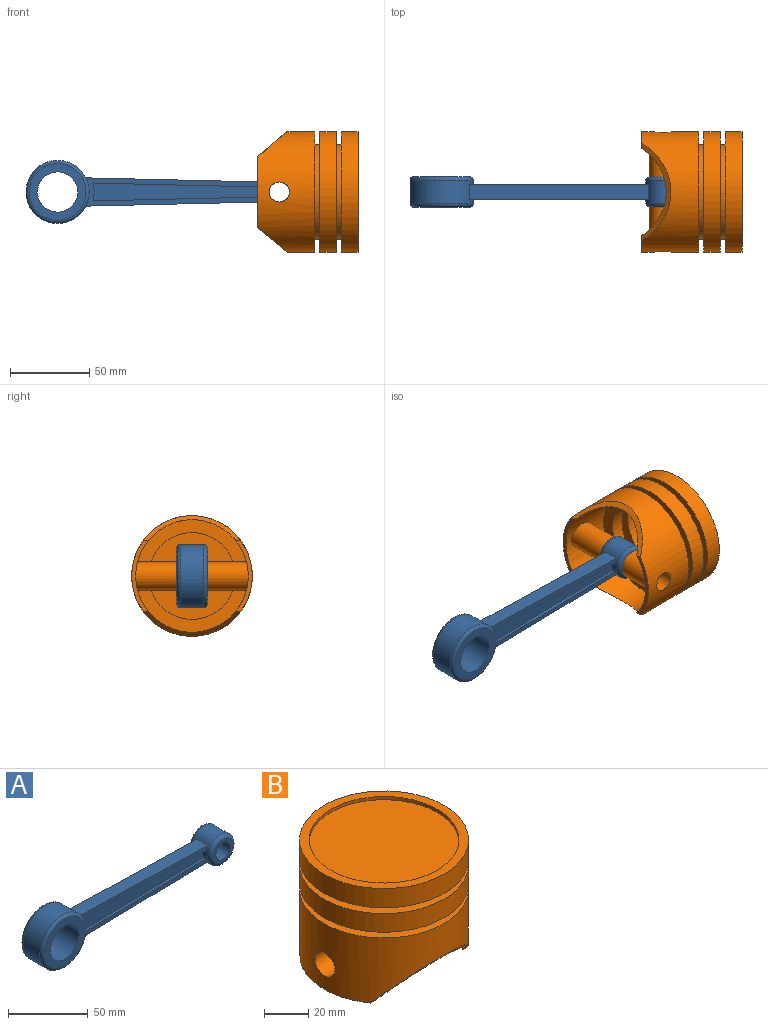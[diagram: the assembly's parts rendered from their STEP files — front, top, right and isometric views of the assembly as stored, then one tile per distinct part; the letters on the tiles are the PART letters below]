
ASSEMBLY  parts=2 mates=1
PART A: 24 faces, bbox 173.8x19.1x43.2 mm
  f0: cylinder r=12.7mm len=25.4mm, axis (0,1,0), area 1520.1mm2, adj f2,f3
  f1: cylinder r=19.95mm len=39.89mm, axis (0,1,0), area 1701.6mm2, adj f4,f5,f6,f7,f16,f17
  f2: plane 35.83x35.83mm, normal (0,-1,0), area 501.5mm2, adj f0,f17
  f3: plane 35.83x35.83mm, normal (0,1,0), area 501.5mm2, adj f0,f16
  f4: plane 113.21x9.53mm, normal (0.02,0,1), area 1078.7mm2, adj f1,f6,f7,f18
  f5: plane 113.21x9.53mm, normal (0.02,0,-1), area 1078.7mm2, adj f1,f6,f7,f18
  f6: plane 113.21x17.87mm, normal (0,-1,0), area 745.9mm2, adj f1,f4,f5,f12,f13,f14,f18
  f7: plane 113.21x17.87mm, normal (0,1,0), area 745.9mm2, adj f1,f4,f5,f8,f9,f10,f18
  f8: plane 107.13x2.49mm, normal (-0.02,0,1), area 217.7mm2, adj f7,f9,f11,f18
  f9: cylinder r=23.12mm len=11.31mm, axis (0,1,0), area 23.2mm2, adj f7,f8,f10,f11
  f10: plane 107.13x2.49mm, normal (-0.02,0,-1), area 217.7mm2, adj f7,f9,f11,f18
  f11: plane 107.13x11.31mm, normal (0,1,0), area 937.4mm2, adj f8,f9,f10,f18
  f12: cylinder r=23.12mm len=11.31mm, axis (0,-1,0), area 23.2mm2, adj f6,f13,f14,f15
  f13: plane 107.13x2.49mm, normal (-0.02,0,1), area 217.7mm2, adj f6,f12,f15,f18
  f14: plane 107.13x2.49mm, normal (-0.02,0,-1), area 217.7mm2, adj f6,f12,f15,f18
  f15: plane 107.13x11.31mm, normal (0,-1,0), area 937.4mm2, adj f12,f13,f14,f18
  f16: torus R=17.91mm, axis (0,-1,0), area 385.2mm2, adj f1,f3
  f17: torus R=17.91mm, axis (0,-1,0), area 385.2mm2, adj f1,f2
  f18: cylinder r=11.11mm len=22.23mm, axis (0,1,0), area 873.8mm2, adj f4,f5,f6,f7,f8,f10,f11,f13
  f19: cylinder r=6.35mm len=19.05mm, axis (0,1,0), area 760.1mm2, adj f20,f21
  f20: plane 17.15x17.15mm, normal (0,-1,0), area 104.2mm2, adj f19,f23
  f21: plane 17.15x17.15mm, normal (0,1,0), area 104.2mm2, adj f19,f22
  f22: torus R=8.57mm, axis (0,-1,0), area 255.4mm2, adj f18,f21
  f23: torus R=8.57mm, axis (0,-1,0), area 255.4mm2, adj f18,f20
PART B: 28 faces, bbox 76.2x76.2x63.5 mm
  f0: plane 44.45x10.34mm, normal (0,0,-1), area 121.2mm2, adj f2,f13,f14,f15
  f1: plane 44.45x10.34mm, normal (0,0,-1), area 121.2mm2, adj f2,f13,f14,f15
  f2: cylinder r=38.1mm len=76.2mm, axis (0,0,-1), area 6640mm2, adj f0,f1,f10,f12,f13,f14
  f3: cylinder r=38.1mm len=76.2mm, axis (0,0,-1), area 2544mm2, adj f4,f5
  f4: plane 76.2x76.2mm, normal (0,0,1), area 975.1mm2, adj f3,f26
  f5: plane 76.2x76.2mm, normal (0,0,-1), area 1735mm2, adj f3,f7
  f6: plane 76.2x76.2mm, normal (0,0,1), area 1735mm2, adj f7,f8
  f7: cylinder r=29.99mm len=59.98mm, axis (0,0,1), area 598.3mm2, adj f5,f6
  f8: cylinder r=38.1mm len=76.2mm, axis (0,0,-1), area 2464.2mm2, adj f6,f9
  f9: plane 76.2x76.2mm, normal (0,0,-1), area 1735mm2, adj f8,f11
  f10: plane 76.2x76.2mm, normal (0,0,1), area 1735mm2, adj f2,f11
  f11: cylinder r=29.99mm len=59.98mm, axis (0,0,1), area 598.3mm2, adj f9,f10
  f12: cylinder r=6.35mm len=76.2mm, axis (1,0,0), area 3019mm2, adj f2
  f13: plane 61.89x18.57mm, normal (0,0.76,-0.65), area 265.8mm2, adj f0,f1,f2,f15
  f14: plane 61.89x18.9mm, normal (0,-0.77,-0.64), area 268.5mm2, adj f0,f1,f2,f15
  f15: cylinder r=35.56mm len=71.12mm, axis (0,0,-1), area 5708.6mm2, adj f0,f1,f13,f14,f23,f25
  f16: cylinder r=35.56mm len=71.12mm, axis (0,0,-1), area 1239.4mm2, adj f17,f18
  f17: plane 71.12x71.12mm, normal (0,0,-1), area 3972.6mm2, adj f16
  f18: plane 71.12x71.12mm, normal (0,0,1), area 1605.5mm2, adj f16,f20
  f19: plane 71.12x71.12mm, normal (0,0,-1), area 1605.5mm2, adj f20,f21
  f20: cylinder r=27.45mm len=54.9mm, axis (0,0,1), area 1423.7mm2, adj f18,f19
  f21: cylinder r=35.56mm len=71.12mm, axis (0,0,-1), area 1164.9mm2, adj f19,f22
  f22: plane 71.12x71.12mm, normal (0,0,1), area 1605.5mm2, adj f21,f24
  f23: plane 71.12x71.12mm, normal (0,0,-1), area 1605.5mm2, adj f15,f24
  f24: cylinder r=27.45mm len=54.9mm, axis (0,0,1), area 1423.7mm2, adj f22,f23
  f25: cylinder r=8.89mm len=71.12mm, axis (1,0,0), area 3909.7mm2, adj f15
  f26: cylinder r=33.78mm len=67.56mm, axis (0,0,1), area 377.4mm2, adj f4,f27
  f27: plane 67.56x67.56mm, normal (0,0,1), area 3585.3mm2, adj f26
PLACE A t=(105.12,-13.82,-15.19)mm
PLACE B rot(axis=(0.58,0.58,0.58),120deg) t=(28.33,-13.82,-15.19)mm
MATE cylindrical A.f18 <-> B.f12  axis (0,1,0) through (42.12,-13.82,-15.19)mm
